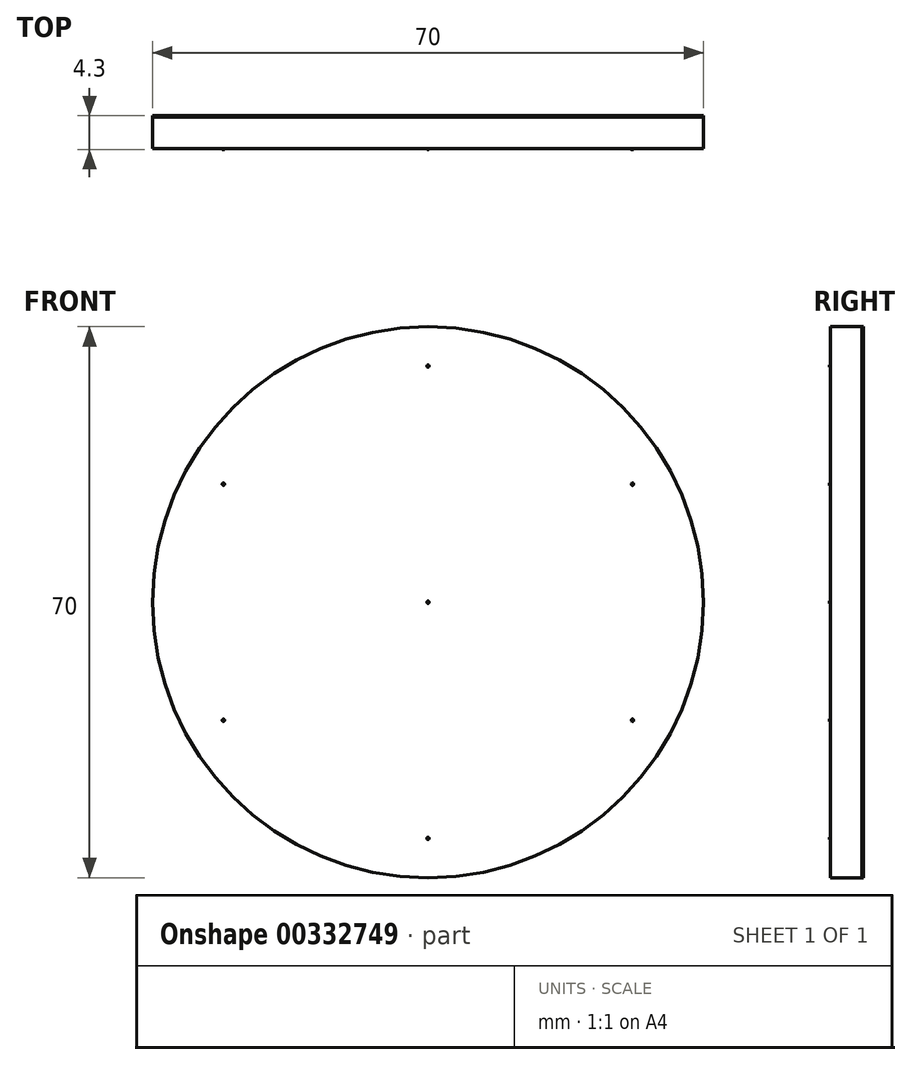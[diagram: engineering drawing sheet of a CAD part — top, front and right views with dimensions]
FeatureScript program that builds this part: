
annotation { "Feature Type Name" : "Feature", "Feature Type Description" : "" }
export const myFeature = defineFeature(function(context is Context, id is Id, definition is map)
    precondition{}
    {
        {
            var Q0;
            Q0=qCreatedBy(makeId("Front.planeOp"),FACE);
            var sketch = newSketch(context, id + "F0", { "sketchPlane" : qUnion([Q0])});
            skCircle(sketch, "E0", {"center": v(0, 0) * mm, "radius": 35 * mm});
            skSolve(sketch);
        }
        {
            var Q0;
            Q0=makeQuery(id+"F0.imprint","IMPRINT",FACE,{"disambiguationData":[TD([[makeQuery(id+"F0.imprint","IMPRINT",EDGE,{"derivedFrom":sQuery(id+"F0.wireOp",EDGE,"E0")}),1.0]])]});
            extrude(context, id + "F1", {"entities" : qUnion([Q0]), "depth" : .2 * mm});
        }
        {
            var Q0;
            Q0=makeQuery(id+"F1.opExtrude","CAP_FACE",FACE,{"disambiguationData":[OSD([sQuery(id+"F0.wireOp",EDGE,"E0")])],"isStart":false});
            var sketch = newSketch(context, id + "F2", { "sketchPlane" : qUnion([Q0])});
            skCircle(sketch, "E1.0", {"center": v(0, 0) * mm, "radius": 35 * mm});
            skSolve(sketch);
        }
        {
            var Q0;
            Q0=makeQuery(id+"F2.imprint","IMPRINT",FACE,{"disambiguationData":[TD([[makeQuery(id+"F2.imprint","IMPRINT",EDGE,{"derivedFrom":sQuery(id+"F2.wireOp",EDGE,"E1.0")}),1.0]])]});
            extrude(context, id + "F3", {"entities" : qUnion([Q0]), "depth" : 4 * mm});
        }
        {
            var Q0;
            Q0=makeQuery(id+"F3.opExtrude","CAP_FACE",FACE,{"disambiguationData":[OSD([sQuery(id+"F2.wireOp",EDGE,"E1.0")])],"isStart":false});
            var sketch = newSketch(context, id + "F4", { "sketchPlane" : qUnion([Q0])});
            skCircle(sketch, "E2", {"center": v(0, 30) * mm, "radius": 0.15 * mm});
            skCircle(sketch, "E3.1.0", {"center": v(-25.98, 15) * mm, "radius": 0.15 * mm});
            skCircle(sketch, "E3.2.0", {"center": v(-25.98, -15) * mm, "radius": 0.15 * mm});
            skCircle(sketch, "E3.3.0", {"center": v(0, -30) * mm, "radius": 0.15 * mm});
            skCircle(sketch, "E3.4.0", {"center": v(25.98, -15) * mm, "radius": 0.15 * mm});
            skCircle(sketch, "E3.5.0", {"center": v(25.98, 15) * mm, "radius": 0.15 * mm});
            skPoint(sketch, "E3.center", {"position": v(0, 0) * mm});
            skCircle(sketch, "E4", {"center": v(0, 0) * mm, "radius": 0.15 * mm});
            skSolve(sketch);
        }
        {
            var Q0;
            Q0 = qSketchRegion(id + "F4", true);
            extrude(context, id + "F5", {"entities" : qUnion([Q0]), "operationType" : NewBodyOperationType.ADD, "depth" : 0.1 * mm});
        }
    });
